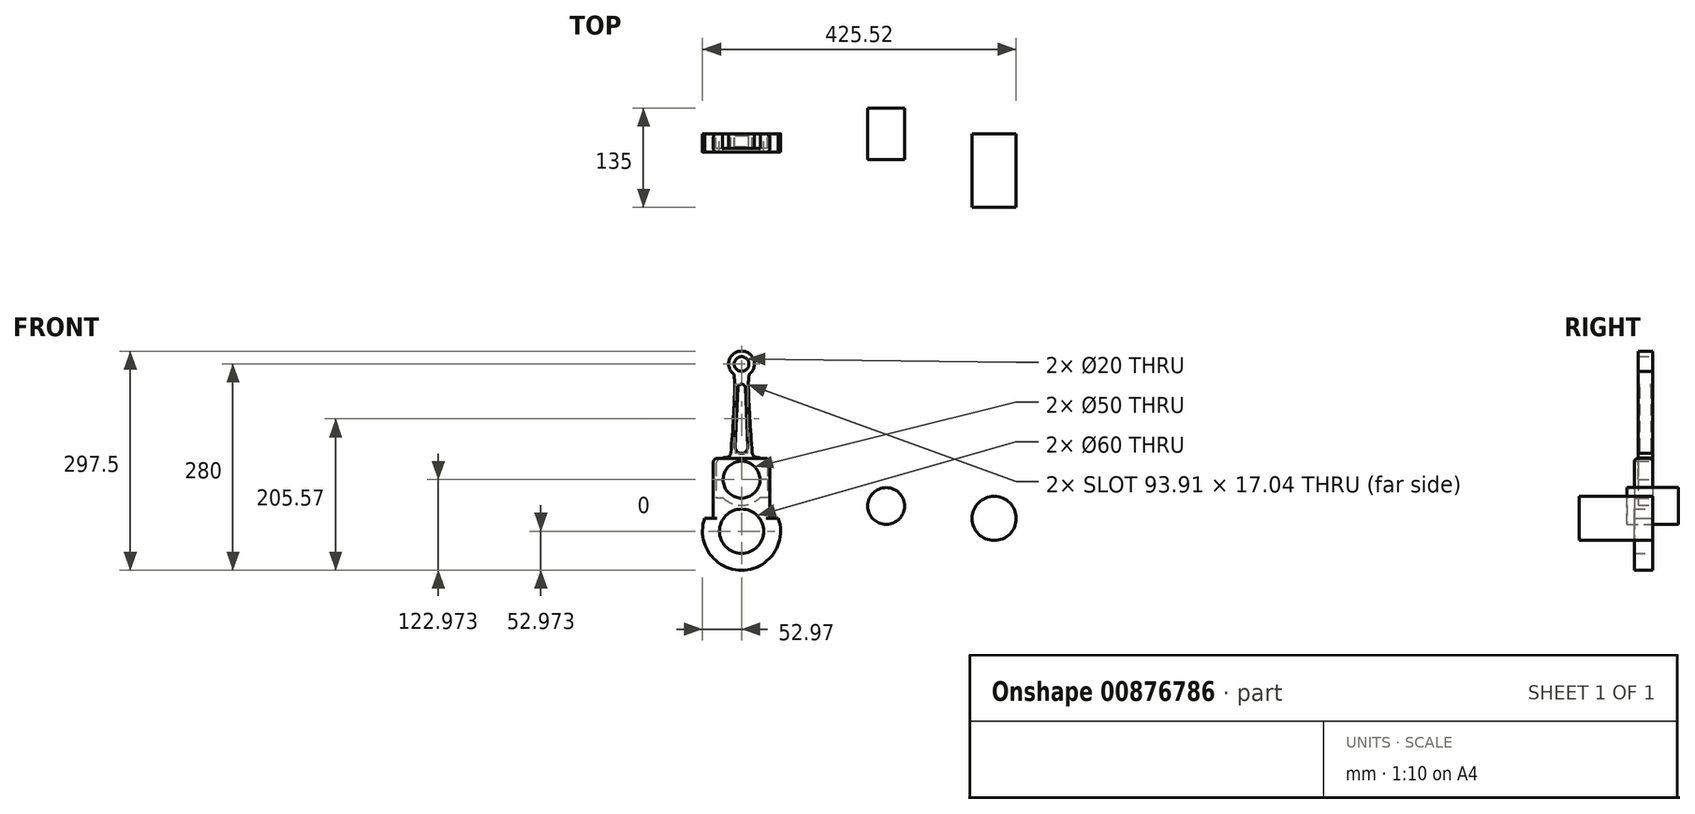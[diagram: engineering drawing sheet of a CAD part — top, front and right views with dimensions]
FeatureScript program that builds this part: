
annotation { "Feature Type Name" : "Feature", "Feature Type Description" : "" }
export const myFeature = defineFeature(function(context is Context, id is Id, definition is map)
    precondition{}
    {
        {
            var Q0;
            Q0=qCreatedBy(makeId("Front.planeOp"),FACE);
            var sketch = newSketch(context, id + "F0", { "sketchPlane" : qUnion([Q0])});
            skCircle(sketch, "E0", {"center": v(0, 0) * mm, "radius": 10 * mm});
            skCircle(sketch, "E1", {"center": v(0, 0) * mm, "radius": 17.5 * mm});
            skPoint(sketch, "E2", {"position": v(-14.4, -9.93) * mm});
            skPoint(sketch, "E3", {"position": v(14.4, -9.93) * mm});
            skFitSpline(sketch, "E4", {"points": [v(-14.4, -9.93) * mm, v(-10.4, -14.54) * mm, v(-14.4, -120.99) * mm], "startDerivative": vector(34.92, -41.2) * mm, "endDerivative": vector(-12.62, -167.2) * mm});
            skFitSpline(sketch, "E5.MirrorCS", {"points": [v(14.4, -9.93) * mm, v(10.4, -14.54) * mm, v(14.4, -120.99) * mm], "startDerivative": vector(-34.92, -41.2) * mm, "endDerivative": vector(12.62, -167.2) * mm});
            skFitSpline(sketch, "E6", {"points": [v(-14.4, -120.99) * mm, v(-17.03, -125.44) * mm, v(-25.89, -127.56) * mm], "startDerivative": vector(-4.13, -10.83) * mm, "endDerivative": vector(-13.6, -2.5) * mm});
            skFitSpline(sketch, "E7.MirrorCS", {"points": [v(14.4, -120.99) * mm, v(17.03, -125.44) * mm, v(25.89, -127.56) * mm], "startDerivative": vector(4.13, -10.83) * mm, "endDerivative": vector(13.6, -2.5) * mm});
            skLineSegment(sketch, "E8", {"start": v(-25.89, -127.56) * mm, "end": v(-35, -127.56) * mm});
            skLineSegment(sketch, "E9.MirrorCS", {"start": v(25.89, -127.56) * mm, "end": v(35, -127.56) * mm});
            skLineSegment(sketch, "E10", {"start": v(-35, -127.56) * mm, "end": v(-35, -157.03) * mm});
            skLineSegment(sketch, "E11.MirrorCS", {"start": v(35, -127.56) * mm, "end": v(35, -157.03) * mm});
            skLineSegment(sketch, "E12", {"start": v(-35, -157.03) * mm, "end": v(-25, -157.03) * mm});
            skLineSegment(sketch, "E13.MirrorCS", {"start": v(35, -157.03) * mm, "end": v(25, -157.03) * mm});
            skArc(sketch, "E14", {"start": v(-25, -157.03) * mm, "mid": v(0, -132.03) * mm, "end": v(25, -157.03) * mm});
            skSolve(sketch);
        }
        {
            var Q0;
            {var subQ6=sQuery(id+"F0.wireOp",EDGE,"E6");Q0=makeQuery(id+"F0.imprint","IMPRINT",FACE,{"disambiguationData":[TD([[makeQuery(id+"F0.imprint","IMPRINT",EDGE,{"derivedFrom":subQ6}),1.0]])]});}
            var Q1;
            Q1=makeQuery(id+"F0.imprint","IMPRINT",FACE,{"disambiguationData":[TD([[makeQuery(id+"F0.imprint","IMPRINT",EDGE,{"derivedFrom":sQuery(id+"F0.wireOp",EDGE,"E0")}),-1.0]])]});
            extrude(context, id + "F1", {"entities" : qUnion([Q0, Q1]), "depth" : 20 * mm, "offsetDistance" : 25 * mm});
        }
        {
            var Q0;
            Q0=qCreatedBy(makeId("Front.planeOp"),FACE);
            var sketch = newSketch(context, id + "F2", { "sketchPlane" : qUnion([Q0])});
            skArc(sketch, "E15", {"start": v(-25, -157.03) * mm, "mid": v(0, -182.03) * mm, "end": v(25, -157.03) * mm});
            skArc(sketch, "E16", {"start": v(-35, -157.03) * mm, "mid": v(0, -192.03) * mm, "end": v(35, -157.03) * mm});
            skLineSegment(sketch, "E17", {"start": v(-35, -157.03) * mm, "end": v(-35, -181.52) * mm});
            skLineSegment(sketch, "E18", {"start": v(-35, -181.52) * mm, "end": v(-25, -181.52) * mm});
            skLineSegment(sketch, "E19.MirrorCS", {"start": v(35, -157.03) * mm, "end": v(35, -181.52) * mm});
            skLineSegment(sketch, "E20.MirrorCS", {"start": v(35, -181.52) * mm, "end": v(25, -181.52) * mm});
            skLineSegment(sketch, "E21", {"start": v(-35, -157.03) * mm, "end": v(-25, -157.03) * mm});
            skLineSegment(sketch, "E22", {"start": v(35, -157.03) * mm, "end": v(25, -157.03) * mm});
            skSolve(sketch);
        }
        {
            var Q0;
            Q0 = qSketchRegion(id + "F2", true);
            extrude(context, id + "F3", {"entities" : qUnion([Q0]), "depth" : 20 * mm, "offsetDistance" : 25 * mm});
        }
        {
            var Q0;
            Q0=makeQuery(id+"F3.boolean.opBoolean","MERGE",FACE,{"derivedFrom":[makeQuery(id+"F1.opExtrude","CAP_FACE",FACE,{"disambiguationData":[OSD([sQuery(id+"F0.wireOp",EDGE,"E0"),sQuery(id+"F0.wireOp",EDGE,"E1"),sQuery(id+"F0.wireOp",EDGE,"E4"),sQuery(id+"F0.wireOp",EDGE,"E5.MirrorCS"),sQuery(id+"F0.wireOp",EDGE,"E6"),sQuery(id+"F0.wireOp",EDGE,"E7.MirrorCS"),sQuery(id+"F0.wireOp",EDGE,"E8"),sQuery(id+"F0.wireOp",EDGE,"E9.MirrorCS"),sQuery(id+"F0.wireOp",EDGE,"E10"),sQuery(id+"F0.wireOp",EDGE,"E11.MirrorCS"),sQuery(id+"F0.wireOp",EDGE,"E12"),sQuery(id+"F0.wireOp",EDGE,"E13.MirrorCS"),sQuery(id+"F0.wireOp",EDGE,"E14")])],"isStart":false}),makeQuery(id+"F3.opExtrude","CAP_FACE",FACE,{"disambiguationData":[OSD([sQuery(id+"F2.wireOp",EDGE,"E15"),sQuery(id+"F2.wireOp",EDGE,"E16"),sQuery(id+"F2.wireOp",EDGE,"E17"),sQuery(id+"F2.wireOp",EDGE,"E18"),sQuery(id+"F2.wireOp",EDGE,"E19.MirrorCS"),sQuery(id+"F2.wireOp",EDGE,"E20.MirrorCS"),sQuery(id+"F2.wireOp",EDGE,"E21"),sQuery(id+"F2.wireOp",EDGE,"E22")])],"isStart":false})]});
            var sketch = newSketch(context, id + "F4", { "sketchPlane" : qUnion([Q0])});
            skArc(sketch, "E23", {"start": v(5.08, -31.72) * mm, "mid": v(0, -27.48) * mm, "end": v(-5.08, -31.72) * mm});
            skLineSegment(sketch, "E24", {"start": v(-5.08, -31.72) * mm, "end": v(-8.52, -113.2) * mm});
            skLineSegment(sketch, "E25.MirrorCS", {"start": v(5.08, -31.72) * mm, "end": v(8.52, -113.2) * mm});
            skArc(sketch, "E26", {"start": v(-8.52, -113.2) * mm, "mid": v(0, -121.38) * mm, "end": v(8.52, -113.2) * mm});
            skSolve(sketch);
        }
        {
            var Q0;
            Q0 = qSketchRegion(id + "F4", true);
            extrude(context, id + "F5", {"entities" : qUnion([Q0]), "operationType" : NewBodyOperationType.REMOVE, "oppositeDirection" : true, "depth" : 2.5 * mm, "offsetDistance" : 25 * mm});
        }
        {
            var Q0;
            Q0=makeQuery(id+"F0.imprint","IMPRINT",FACE,{"disambiguationData":[TD([[makeQuery(id+"F0.imprint","IMPRINT",EDGE,{"derivedFrom":sQuery(id+"F0.wireOp",EDGE,"E0")}),-1.0]])]});
            var sketch = newSketch(context, id + "F6", { "sketchPlane" : qUnion([Q0])});
            skArc(sketch, "E27", {"start": v(5.08, -31.72) * mm, "mid": v(0, -27.48) * mm, "end": v(-5.08, -31.72) * mm});
            skLineSegment(sketch, "E28", {"start": v(-5.08, -31.72) * mm, "end": v(-8.52, -113.2) * mm});
            skLineSegment(sketch, "E29", {"start": v(5.08, -31.72) * mm, "end": v(8.52, -113.2) * mm});
            skArc(sketch, "E30", {"start": v(-8.52, -113.2) * mm, "mid": v(0, -121.38) * mm, "end": v(8.52, -113.2) * mm});
            skSolve(sketch);
        }
        {
            var Q0;
            Q0 = qSketchRegion(id + "F6", true);
            extrude(context, id + "F7", {"entities" : qUnion([Q0]), "operationType" : NewBodyOperationType.REMOVE, "depth" : 2.5 * mm, "offsetDistance" : 25 * mm});
        }
        {
            var Q0;
            Q0=qCreatedBy(makeId("Front.planeOp"),FACE);
            var sketch = newSketch(context, id + "F8", { "sketchPlane" : qUnion([Q0])});
            skCircle(sketch, "E31", {"center": v(0, -157.03) * mm, "radius": 25 * mm});
            skCircle(sketch, "E32", {"center": v(0, -227.03) * mm, "radius": 30 * mm});
            skLineSegment(sketch, "E33", {"start": v(33.25, -128.3) * mm, "end": v(-33.25, -128.3) * mm});
            skLineSegment(sketch, "E34", {"start": v(-38.25, -133.3) * mm, "end": v(-38.25, -209.6) * mm});
            skLineSegment(sketch, "E35", {"start": v(-38.25, -209.6) * mm, "end": v(-50.02, -209.6) * mm});
            skLineSegment(sketch, "E36.MirrorCS", {"start": v(38.25, -133.3) * mm, "end": v(38.25, -209.6) * mm});
            skLineSegment(sketch, "E37.MirrorCS", {"start": v(38.25, -209.6) * mm, "end": v(50.02, -209.6) * mm});
            skArc(sketch, "E38", {"start": v(-50.02, -209.6) * mm, "mid": v(0, -280) * mm, "end": v(50.02, -209.6) * mm});
            skPoint(sketch, "E39.visualSharp", {"position": v(-38.25, -128.3) * mm});
            skArc(sketch, "E39.filletArc", {"start": v(-33.25, -128.3) * mm, "mid": v(-36.78, -129.76) * mm, "end": v(-38.25, -133.3) * mm});
            skPoint(sketch, "E40.visualSharp", {"position": v(38.25, -128.3) * mm});
            skArc(sketch, "E40.filletArc", {"start": v(38.25, -133.3) * mm, "mid": v(36.78, -129.76) * mm, "end": v(33.25, -128.3) * mm});
            skSolve(sketch);
        }
        {
            var Q0;
            Q0 = qSketchRegion(id + "F8", true);
            extrude(context, id + "F9", {"entities" : qUnion([Q0]), "depth" : 25 * mm, "offsetDistance" : 25 * mm});
        }
        {
            var Q0;
            Q0=qCreatedBy(makeId("Front.planeOp"),FACE);
            var sketch = newSketch(context, id + "F10", { "sketchPlane" : qUnion([Q0])});
            skCircle(sketch, "E41", {"center": v(196.16, -192.85) * mm, "radius": 24.95 * mm});
            skSolve(sketch);
        }
        {
            var Q0;
            Q0=makeQuery(id+"F10.imprint","IMPRINT",FACE,{"disambiguationData":[TD([[makeQuery(id+"F10.imprint","IMPRINT",EDGE,{"derivedFrom":sQuery(id+"F10.wireOp",EDGE,"E41")}),1.0]])]});
            extrude(context, id + "F11", {"entities" : qUnion([Q0]), "endBound" : BoundingType.SYMMETRIC, "depth" : 70 * mm, "offsetDistance" : 25 * mm});
        }
        {
            var Q0;
            Q0=qCreatedBy(makeId("Front.planeOp"),FACE);
            var sketch = newSketch(context, id + "F12", { "sketchPlane" : qUnion([Q0])});
            skCircle(sketch, "E42", {"center": v(342.55, -209.6) * mm, "radius": 30 * mm});
            skSolve(sketch);
        }
        {
            var Q0;
            Q0=makeQuery(id+"F12.imprint","IMPRINT",FACE,{"disambiguationData":[TD([[makeQuery(id+"F12.imprint","IMPRINT",EDGE,{"derivedFrom":sQuery(id+"F12.wireOp",EDGE,"E42")}),1.0]])]});
            extrude(context, id + "F13", {"entities" : qUnion([Q0]), "depth" : 100 * mm, "offsetDistance" : 25 * mm});
        }
        {
            var Q0;
            Q0=makeQuery(id+"F9.opExtrude","CAP_EDGE",EDGE,{"disambiguationData":[OSD([sQuery(id+"F8.wireOp",EDGE,"E39.filletArc")])],"isStart":false});
            var Q1;
            Q1=makeQuery(id+"F9.opExtrude","CAP_EDGE",EDGE,{"disambiguationData":[OSD([sQuery(id+"F8.wireOp",EDGE,"E33")])],"isStart":true});
            fillet(context, id + "F14", {"entities" : qUnion([Q0, Q1]), "radius" : 5 * mm, "tangentPropagation" : true, "allowEdgeOverflow" : false});
        }
        {
            var Q0;
            Q0=makeQuery(id+"F1.opExtrude","SWEPT_EDGE",EDGE,{"disambiguationData":[OSD([sQuery(id+"F0.wireOp",EDGE,"E9.MirrorCS"),sQuery(id+"F0.wireOp",EDGE,"E11.MirrorCS")])]});
            var Q1;
            {var subQ0=sQuery(id+"F0.wireOp",EDGE,"E10");var subQ1=sQuery(id+"F0.wireOp",EDGE,"E8");Q1=makeQuery(id+"FvwaBBJAEEir725_2.hole-0.boolean.opBoolean","SPLIT",EDGE,{"disambiguationData":[TD([makeQuery(id+"F1.opExtrude","CAP_FACE",FACE,{"disambiguationData":[OSD([sQuery(id+"F0.wireOp",EDGE,"E0"),sQuery(id+"F0.wireOp",EDGE,"E1"),sQuery(id+"F0.wireOp",EDGE,"E4"),sQuery(id+"F0.wireOp",EDGE,"E5.MirrorCS"),sQuery(id+"F0.wireOp",EDGE,"E6"),sQuery(id+"F0.wireOp",EDGE,"E7.MirrorCS"),subQ1,sQuery(id+"F0.wireOp",EDGE,"E9.MirrorCS"),subQ0,sQuery(id+"F0.wireOp",EDGE,"E11.MirrorCS"),sQuery(id+"F0.wireOp",EDGE,"E12"),sQuery(id+"F0.wireOp",EDGE,"E13.MirrorCS"),sQuery(id+"F0.wireOp",EDGE,"E14")])],"isStart":false})])],"derivedFrom":makeQuery(id+"F1.opExtrude","SWEPT_EDGE",EDGE,{"disambiguationData":[OSD([subQ1,subQ0])]})});}
            var Q2;
            {var subQ0=sQuery(id+"F0.wireOp",EDGE,"E10");var subQ1=sQuery(id+"F0.wireOp",EDGE,"E8");Q2=makeQuery(id+"FvwaBBJAEEir725_2.hole-0.boolean.opBoolean","SPLIT",EDGE,{"disambiguationData":[TD([makeQuery(id+"F1.opExtrude","CAP_FACE",FACE,{"disambiguationData":[OSD([sQuery(id+"F0.wireOp",EDGE,"E0"),sQuery(id+"F0.wireOp",EDGE,"E1"),sQuery(id+"F0.wireOp",EDGE,"E4"),sQuery(id+"F0.wireOp",EDGE,"E5.MirrorCS"),sQuery(id+"F0.wireOp",EDGE,"E6"),sQuery(id+"F0.wireOp",EDGE,"E7.MirrorCS"),subQ1,sQuery(id+"F0.wireOp",EDGE,"E9.MirrorCS"),subQ0,sQuery(id+"F0.wireOp",EDGE,"E11.MirrorCS"),sQuery(id+"F0.wireOp",EDGE,"E12"),sQuery(id+"F0.wireOp",EDGE,"E13.MirrorCS"),sQuery(id+"F0.wireOp",EDGE,"E14")])],"isStart":true})])],"derivedFrom":makeQuery(id+"F1.opExtrude","SWEPT_EDGE",EDGE,{"disambiguationData":[OSD([subQ1,subQ0])]})});}
            fillet(context, id + "F15", {"entities" : qUnion([Q0, Q1, Q2]), "radius" : 10 * mm, "tangentPropagation" : true, "allowEdgeOverflow" : false});
        }
    });
